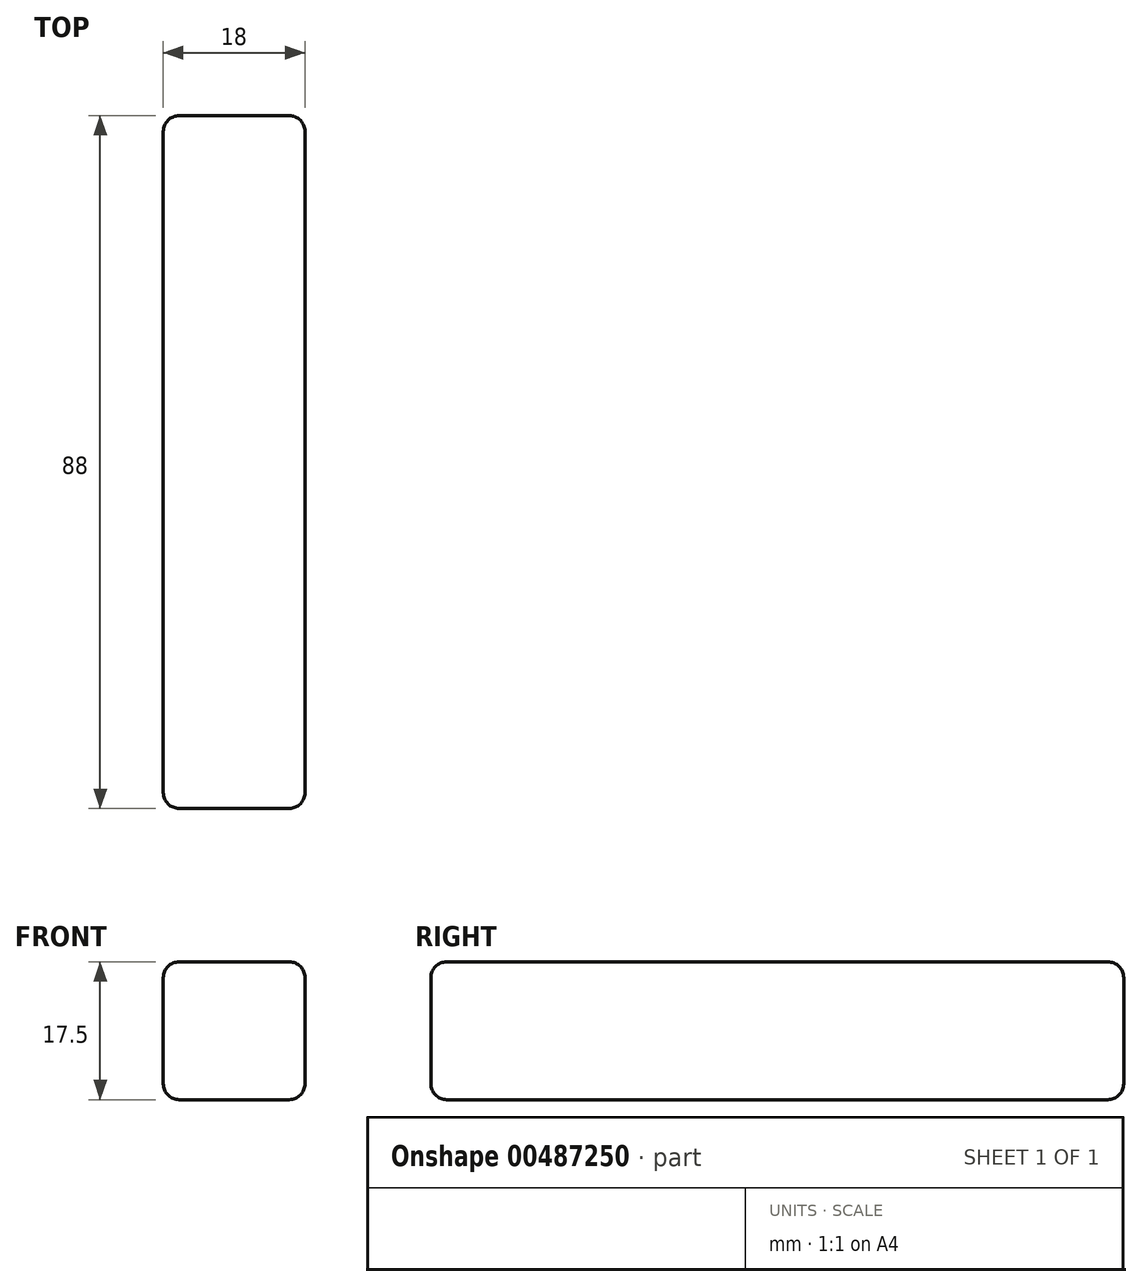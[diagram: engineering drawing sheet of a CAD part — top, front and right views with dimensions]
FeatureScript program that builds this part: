
annotation { "Feature Type Name" : "Feature", "Feature Type Description" : "" }
export const myFeature = defineFeature(function(context is Context, id is Id, definition is map)
    precondition{}
    {
        {
            var Q0;
            Q0=qCreatedBy(makeId("Top.planeOp"),FACE);
            var sketch = newSketch(context, id + "F0", { "sketchPlane" : qUnion([Q0])});
            skLineSegment(sketch, "E0.bottom", {"start": v(-9, 44) * mm, "end": v(9, 44) * mm});
            skLineSegment(sketch, "E0.top", {"start": v(-9, -44) * mm, "end": v(9, -44) * mm});
            skLineSegment(sketch, "E0.left", {"start": v(-9, 44) * mm, "end": v(-9, -44) * mm});
            skLineSegment(sketch, "E0.right", {"start": v(9, 44) * mm, "end": v(9, -44) * mm});
            skPoint(sketch, "E0.middle", {"position": v(0, 0) * mm});
            skSolve(sketch);
        }
        {
            var Q0;
            Q0 = qSketchRegion(id + "F0", true);
            extrude(context, id + "F1", {"entities" : qUnion([Q0]), "endBound" : BoundingType.SYMMETRIC, "depth" : 17.5 * mm});
        }
        {
            var Q0;
            Q0=makeQuery(id+"F1.opExtrude","CAP_EDGE",EDGE,{"disambiguationData":[OSD([sQuery(id+"F0.wireOp",EDGE,"E0.right")])],"isStart":true});
            var Q1;
            Q1=makeQuery(id+"F1.opExtrude","CAP_EDGE",EDGE,{"disambiguationData":[OSD([sQuery(id+"F0.wireOp",EDGE,"E0.left")])],"isStart":true});
            var Q2;
            Q2=makeQuery(id+"F1.opExtrude","CAP_EDGE",EDGE,{"disambiguationData":[OSD([sQuery(id+"F0.wireOp",EDGE,"E0.right")])],"isStart":false});
            var Q3;
            Q3=makeQuery(id+"F1.opExtrude","CAP_EDGE",EDGE,{"disambiguationData":[OSD([sQuery(id+"F0.wireOp",EDGE,"E0.left")])],"isStart":false});
            var Q4;
            Q4=makeQuery(id+"F1.opExtrude","CAP_EDGE",EDGE,{"disambiguationData":[OSD([sQuery(id+"F0.wireOp",EDGE,"E0.top")])],"isStart":false});
            var Q5;
            Q5=makeQuery(id+"F1.opExtrude","SWEPT_EDGE",EDGE,{"disambiguationData":[OSD([sQuery(id+"F0.wireOp",EDGE,"E0.top"),sQuery(id+"F0.wireOp",EDGE,"E0.left")])]});
            var Q6;
            Q6=makeQuery(id+"F1.opExtrude","CAP_EDGE",EDGE,{"disambiguationData":[OSD([sQuery(id+"F0.wireOp",EDGE,"E0.top")])],"isStart":true});
            var Q7;
            Q7=makeQuery(id+"F1.opExtrude","SWEPT_EDGE",EDGE,{"disambiguationData":[OSD([sQuery(id+"F0.wireOp",EDGE,"E0.top"),sQuery(id+"F0.wireOp",EDGE,"E0.right")])]});
            var Q8;
            Q8=makeQuery(id+"F1.opExtrude","SWEPT_EDGE",EDGE,{"disambiguationData":[OSD([sQuery(id+"F0.wireOp",EDGE,"E0.bottom"),sQuery(id+"F0.wireOp",EDGE,"E0.right")])]});
            var Q9;
            Q9=makeQuery(id+"F1.opExtrude","CAP_EDGE",EDGE,{"disambiguationData":[OSD([sQuery(id+"F0.wireOp",EDGE,"E0.bottom")])],"isStart":true});
            var Q10;
            Q10=makeQuery(id+"F1.opExtrude","SWEPT_EDGE",EDGE,{"disambiguationData":[OSD([sQuery(id+"F0.wireOp",EDGE,"E0.bottom"),sQuery(id+"F0.wireOp",EDGE,"E0.left")])]});
            var Q11;
            Q11=makeQuery(id+"F1.opExtrude","CAP_EDGE",EDGE,{"disambiguationData":[OSD([sQuery(id+"F0.wireOp",EDGE,"E0.bottom")])],"isStart":false});
            fillet(context, id + "F2", {"entities" : qUnion([Q0, Q1, Q2, Q3, Q4, Q5, Q6, Q7, Q8, Q9, Q10, Q11]), "radius" : 2 * mm, "tangentPropagation" : true, "allowEdgeOverflow" : false});
        }
    });
